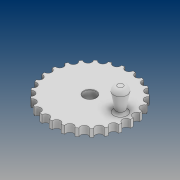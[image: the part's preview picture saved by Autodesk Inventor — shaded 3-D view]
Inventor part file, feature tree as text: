
AUTODESK INVENTOR PART (.ipt)
format: ipt  version: 2021 (Build 250183000, 183)  size: 257,024 bytes
history: native  units: mm
features: sketch x4, extrude x3, fillet x3, pattern_circular x1, plane x1, loft x1, projected_geometry x1
ambient origin geometry x8: Origin, YZ Plane, XZ Plane, XY Plane, X Axis, Y Axis, Z Axis, Center Point
bodies: Solid1 (feature_tree)
feature tree (14):
  sketch  "Sketch1"  dims[d0=7.8mm d1=5.0mm]
  extrude  "Extrusion1"  Depth=5.0mm
  extrude  "Extrusion2"  Depth=5.0mm
  extrude  "Extrusion3"  Depth=5.0mm TaperAngle=0.0deg
  pattern_circular  "Circular Pattern1"  [2 undecoded]
  fillet  "Fillet1"  Radius=2.5mm
  sketch  "Sketch3"  dims[d5=250.0mm d7=360.0deg d9=5.0mm d10=0.0mm]
  plane  "Work Plane1"
  loft  "Loft1"
  fillet  "Fillet2"  Radius=2.8mm
  fillet  "Fillet3"  Radius=20.0mm
  sketch  "Sketch2"  dims[d3=55.0mm d4=5.0mm]
  projected_geometry  "Projected Loop1"
  sketch  "Sketch4"  dims[d11=5.0mm d12=0.0mm d13=8.0mm d14=2.5mm d15=10.5mm d16=0.0mm d17=2.8mm d18=20.0mm d19=90.0deg d21=0.25mm d22=20.0mm d23=5.0mm d24=15.0mm d25=10.0mm d26=0.0mm d27=90.0deg d28=0.0mm d29=90.0deg d30=1.5mm d31=2.75mm]
note: 2 required parameter values undecoded (feature->parameter linkage not recoverable at this tier; creation-order binding heuristic only, values carry confidence <= 0.55)
